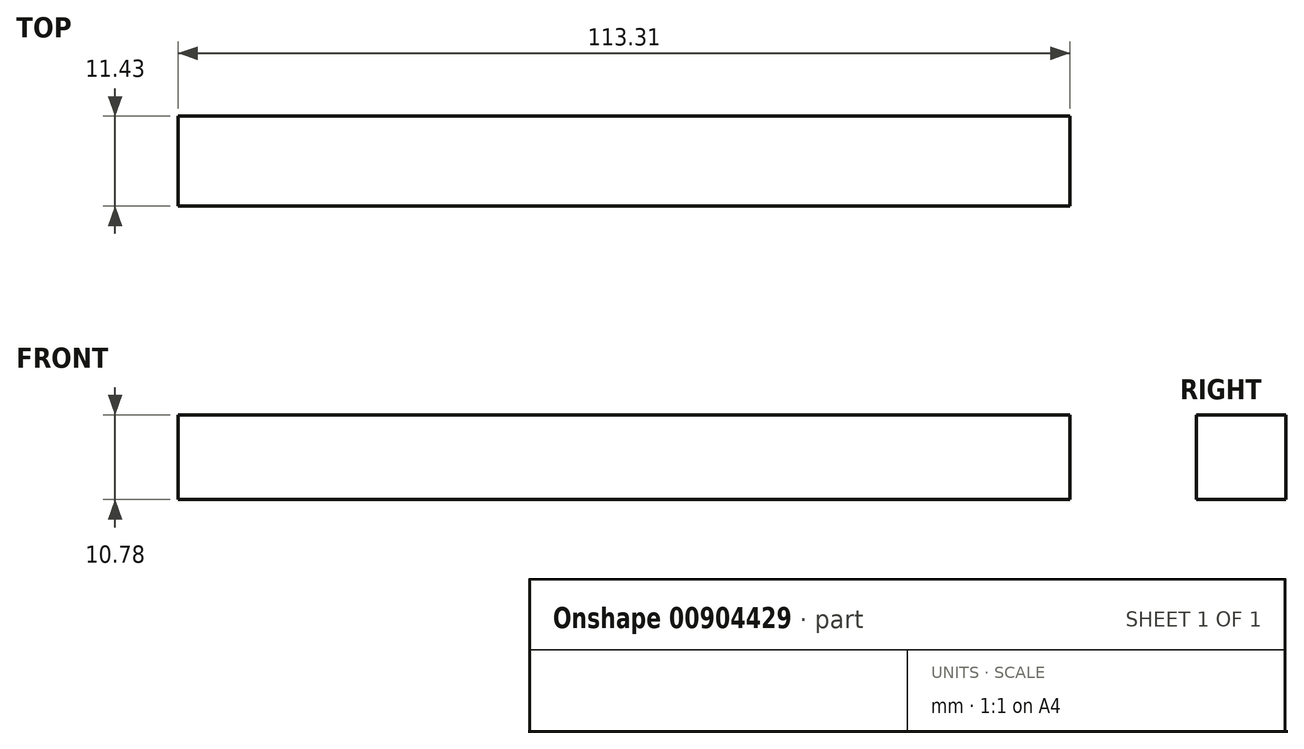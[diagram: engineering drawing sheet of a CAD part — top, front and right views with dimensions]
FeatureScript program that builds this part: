
annotation { "Feature Type Name" : "Feature", "Feature Type Description" : "" }
export const myFeature = defineFeature(function(context is Context, id is Id, definition is map)
    precondition{}
    {
        {
            var Q0;
            Q0=qCreatedBy(makeId("Front.planeOp"),FACE);
            var sketch = newSketch(context, id + "F0", { "sketchPlane" : qUnion([Q0])});
            skLineSegment(sketch, "E0.bottom", {"start": v(-56.55, 38.74) * mm, "end": v(56.76, 38.74) * mm});
            skLineSegment(sketch, "E0.top", {"start": v(-56.55, 27.96) * mm, "end": v(56.76, 27.96) * mm});
            skLineSegment(sketch, "E0.left", {"start": v(-56.55, 38.74) * mm, "end": v(-56.55, 27.96) * mm});
            skLineSegment(sketch, "E0.right", {"start": v(56.76, 38.74) * mm, "end": v(56.76, 27.96) * mm});
            skSolve(sketch);
        }
        {
            var Q0;
            Q0=makeQuery(id+"F0.imprint","IMPRINT",FACE,{"disambiguationData":[TD([[makeQuery(id+"F0.imprint","IMPRINT",EDGE,{"derivedFrom":sQuery(id+"F0.wireOp",EDGE,"E0.bottom")}),-1.0]])]});
            extrude(context, id + "F1", {"entities" : qUnion([Q0]), "depth" : 11.43 * mm, "offsetDistance" : 25.4 * mm});
        }
    });
